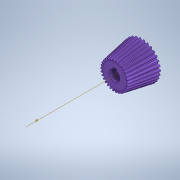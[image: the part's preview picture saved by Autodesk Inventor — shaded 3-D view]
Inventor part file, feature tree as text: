
AUTODESK INVENTOR PART (.ipt)
format: ipt  version: 2021 (Build 250183000, 183)  size: 685,056 bytes
history: native  units: mm
features: other x24, loft x2, pattern_circular x2, sketch x2, extrude x1
ambient origin geometry x6: Origin, XZ Plane, X Axis, Y Axis, Z Axis, Center Point
bodies: Solid1 (feature_tree)
feature tree (31):
  other  "Top Point"
  other  "Mesh Plane2"
  other  "Teeth Body"
  other  "Start Point"
  other  "Tooth Plane"
  other  "Start Sketch"
  other  "End Point"
  other  "3D Sketch Right"
  other  "End Plane Right"
  loft  "Loft Right"
  pattern_circular  "Circular Pattern Right"  [2 undecoded]
  other  "3D Sketch Left"
  other  "End Plane Left"
  loft  "Loft Left"
  pattern_circular  "Circular Pattern Left"  Angle=90.0deg  [1 undecoded]
  other  "Fix Body"
  extrude  "Extrusion1"  Depth=3.175mm
  other  "Mesh Plane"
  other  "Top Plane"
  other  "Teeth Body Sketch"
  other  "End Plane"
  other  "End Sketch"
  other  "Helical Curve Left"
  other  "End Sketch Left"
  other  "Body Sketch"
  sketch  "Sketch6"  dims[d0=31.75mm d1=29.244559mm]
  other  "Srf1"
  other  "Helical Curve Right"
  other  "End Sketch Right"
  sketch  "Sketch8"  dims[d2=33.837867mm d3=25.4mm d4=95.076011mm d5=90.0deg d7=5.865417mm d8=6.223675mm d9=13.765897mm d11=25.516417mm d12=4.315516mm d15=4.579106mm d16=10.128341mm d17=0.0mm d18=90.0deg d19=0.0mm d20=90.0deg d21=300.0mm d22=360.0deg d26=391.538189mm d27=25.169238mm d28=31.75mm d29=-1.651487mm d30=4.315516mm d31=4.579106mm d32=10.128341mm d35=0.0mm d37=0.0mm d39=0.0mm d40=90.0deg d41=300.0mm d42=360.0deg d46=90.0deg d47=90.0deg d48=0.0mm d49=0.0mm d50=90.0deg d51=1.047198mm d52=0.0mm d53=0.0mm d54=0.0mm d56=12.299245mm d57=17.850809mm d58=14.544576mm d59=13.13384mm d60=10.701259mm d61=13.13384mm d62=10.701259mm d63=90.0deg d64=90.0deg d65=391.538189mm d66=31.5mm d67=31.75mm d68=-1.651487mm d69=25.169238mm d70=4.579106mm d71=10.128341mm d72=4.315516mm d73=10.701259mm d74=13.13384mm d75=0.0mm d76=90.0deg d77=0.0mm d78=90.0deg d79=0.0mm d80=90.0deg d81=300.0mm d82=360.0deg d84=10.0mm d85=20.0mm d86=20.0mm d87=10.0mm d88=0.0mm d89=0.0mm d90=9.525mm d91=0.0mm d92=0.0mm d95=1.190625mm d96=3.175mm]
  other  "Pitch Diameter"
note: 3 required parameter values undecoded (feature->parameter linkage not recoverable at this tier; creation-order binding heuristic only, values carry confidence <= 0.55)
